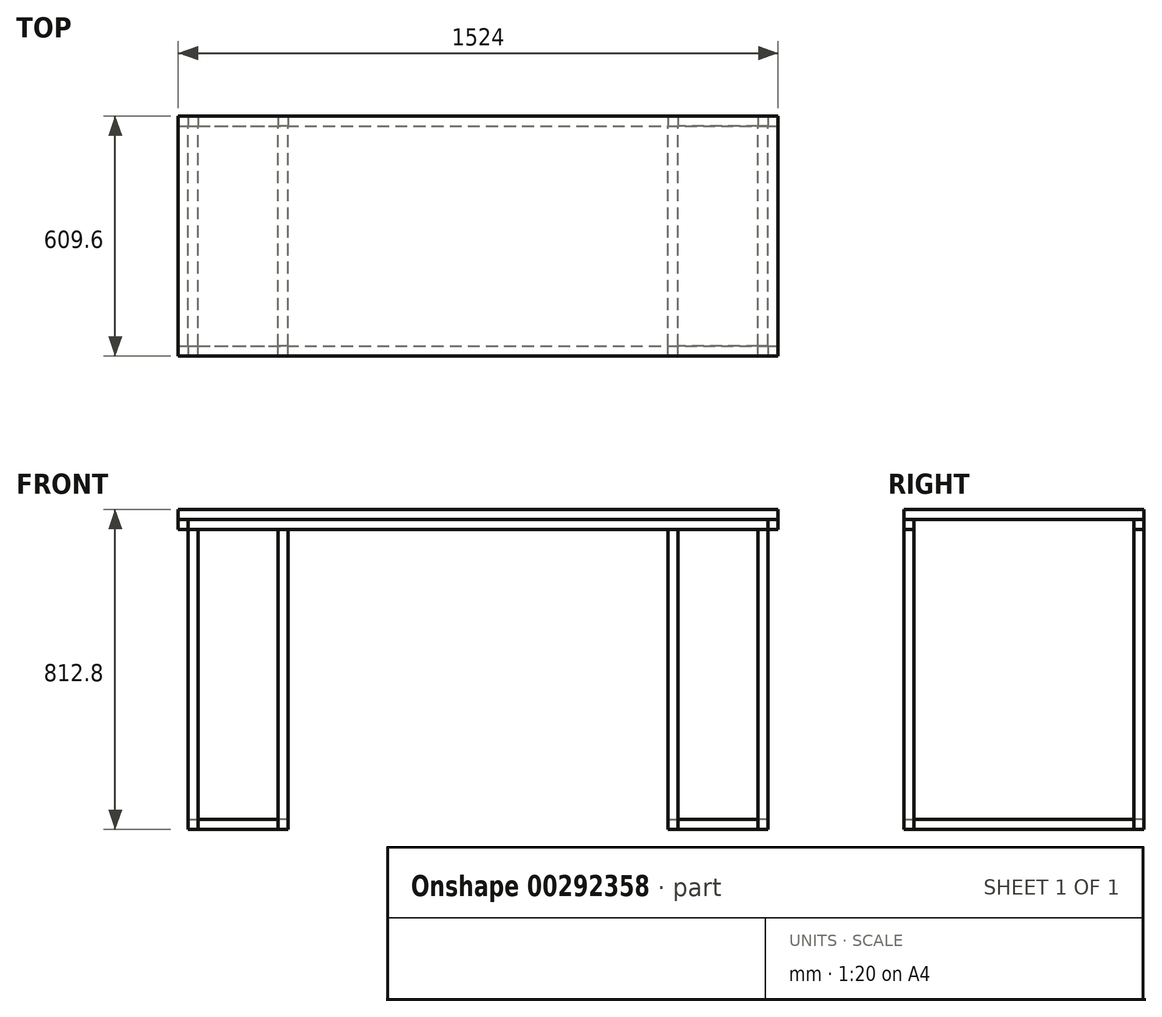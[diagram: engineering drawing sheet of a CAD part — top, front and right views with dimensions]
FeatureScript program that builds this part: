
annotation { "Feature Type Name" : "Feature", "Feature Type Description" : "" }
export const myFeature = defineFeature(function(context is Context, id is Id, definition is map)
    precondition{}
    {
        {
            var Q0;
            Q0=qCreatedBy(makeId("Top.planeOp"),FACE);
            var sketch = newSketch(context, id + "F0", { "sketchPlane" : qUnion([Q0])});
            skLineSegment(sketch, "E0.bottom", {"start": v(-1219.74, 156.93) * mm, "end": v(304.26, 156.93) * mm});
            skLineSegment(sketch, "E0.top", {"start": v(-1219.74, -452.67) * mm, "end": v(304.26, -452.67) * mm});
            skLineSegment(sketch, "E0.left", {"start": v(-1219.74, 156.93) * mm, "end": v(-1219.74, -452.67) * mm});
            skLineSegment(sketch, "E0.right", {"start": v(304.26, 156.93) * mm, "end": v(304.26, -452.67) * mm});
            skSolve(sketch);
        }
        {
            var Q0;
            Q0 = qSketchRegion(id + "F0", true);
            extrude(context, id + "F1", {"entities" : qUnion([Q0]), "depth" : 25.4 * mm});
        }
        {
            var Q0;
            Q0=makeQuery(id+"F1.opExtrude","CAP_FACE",FACE,{"disambiguationData":[OSD([sQuery(id+"F0.wireOp",EDGE,"E0.bottom"),sQuery(id+"F0.wireOp",EDGE,"E0.top"),sQuery(id+"F0.wireOp",EDGE,"E0.left"),sQuery(id+"F0.wireOp",EDGE,"E0.right")])],"isStart":true});
            var sketch = newSketch(context, id + "F2", { "sketchPlane" : qUnion([Q0])});
            skLineSegment(sketch, "E1.bottom", {"start": v(-1219.74, 452.67) * mm, "end": v(304.26, 452.67) * mm});
            skLineSegment(sketch, "E1.top", {"start": v(-1219.74, 427.27) * mm, "end": v(304.26, 427.27) * mm});
            skLineSegment(sketch, "E1.left", {"start": v(-1219.74, 452.67) * mm, "end": v(-1219.74, 427.27) * mm});
            skLineSegment(sketch, "E1.right", {"start": v(304.26, 452.67) * mm, "end": v(304.26, 427.27) * mm});
            skLineSegment(sketch, "E2.bottom", {"start": v(-1219.74, -156.93) * mm, "end": v(304.26, -156.93) * mm});
            skLineSegment(sketch, "E2.top", {"start": v(-1219.74, -131.53) * mm, "end": v(304.26, -131.53) * mm});
            skLineSegment(sketch, "E2.left", {"start": v(-1219.74, -156.93) * mm, "end": v(-1219.74, -131.53) * mm});
            skLineSegment(sketch, "E2.right", {"start": v(304.26, -156.93) * mm, "end": v(304.26, -131.53) * mm});
            skLineSegment(sketch, "E3.bottom", {"start": v(-1219.74, 427.27) * mm, "end": v(-1194.34, 427.27) * mm});
            skLineSegment(sketch, "E3.top", {"start": v(-1219.74, -131.53) * mm, "end": v(-1194.34, -131.53) * mm});
            skLineSegment(sketch, "E3.left", {"start": v(-1219.74, 427.27) * mm, "end": v(-1219.74, -131.53) * mm});
            skLineSegment(sketch, "E3.right", {"start": v(-1194.34, 427.27) * mm, "end": v(-1194.34, -131.53) * mm});
            skLineSegment(sketch, "E4.bottom", {"start": v(278.86, 427.27) * mm, "end": v(304.26, 427.27) * mm});
            skLineSegment(sketch, "E4.top", {"start": v(278.86, -131.53) * mm, "end": v(304.26, -131.53) * mm});
            skLineSegment(sketch, "E4.left", {"start": v(278.86, 427.27) * mm, "end": v(278.86, -131.53) * mm});
            skLineSegment(sketch, "E4.right", {"start": v(304.26, 427.27) * mm, "end": v(304.26, -131.53) * mm});
            skLineSegment(sketch, "E5", {"start": v(-1194.34, -131.53) * mm, "end": v(-1194.34, -156.93) * mm});
            skLineSegment(sketch, "E6", {"start": v(-1194.34, 427.27) * mm, "end": v(-1194.34, 452.67) * mm});
            skLineSegment(sketch, "E7", {"start": v(278.86, 427.27) * mm, "end": v(278.86, 452.67) * mm});
            skLineSegment(sketch, "E8", {"start": v(278.86, -131.53) * mm, "end": v(278.86, -156.93) * mm});
            skSolve(sketch);
        }
        {
            var Q0;
            Q0=makeQuery(id+"F2.imprint","IMPRINT",FACE,{"disambiguationData":[TD([[makeQuery(id+"F2.imprint","IMPRINT",EDGE,{"derivedFrom":sQuery(id+"F2.wireOp",EDGE,"E2.top")}),-1.0]])]});
            var Q1;
            Q1=makeQuery(id+"F2.imprint","IMPRINT",FACE,{"disambiguationData":[TD([[makeQuery(id+"F2.imprint","IMPRINT",EDGE,{"derivedFrom":sQuery(id+"F2.wireOp",EDGE,"E1.top")}),1.0]])]});
            extrude(context, id + "F3", {"entities" : qUnion([Q0, Q1]), "depth" : 25.4 * mm});
        }
        {
            var Q0;
            Q0=makeQuery(id+"F2.imprint","IMPRINT",FACE,{"disambiguationData":[TD([[makeQuery(id+"F2.imprint","IMPRINT",EDGE,{"derivedFrom":sQuery(id+"F2.wireOp",EDGE,"E3.bottom")}),-1.0]])]});
            var Q1;
            Q1=makeQuery(id+"F2.imprint","IMPRINT",FACE,{"disambiguationData":[TD([[makeQuery(id+"F2.imprint","IMPRINT",EDGE,{"derivedFrom":sQuery(id+"F2.wireOp",EDGE,"E4.bottom")}),-1.0]])]});
            var Q2;
            {var subQ0=sQuery(id+"F2.wireOp",EDGE,"E1.left");Q2=makeQuery(id+"F2.imprint","IMPRINT",FACE,{"disambiguationData":[TD([[makeQuery(id+"F2.imprint","IMPRINT",EDGE,{"derivedFrom":subQ0}),-1.0]])]});}
            var Q3;
            {var subQ0=sQuery(id+"F2.wireOp",EDGE,"E2.left");Q3=makeQuery(id+"F2.imprint","IMPRINT",FACE,{"disambiguationData":[TD([[makeQuery(id+"F2.imprint","IMPRINT",EDGE,{"derivedFrom":subQ0}),-1.0]])]});}
            var Q4;
            {var subQ0=sQuery(id+"F2.wireOp",EDGE,"E2.right");Q4=makeQuery(id+"F2.imprint","IMPRINT",FACE,{"disambiguationData":[TD([[makeQuery(id+"F2.imprint","IMPRINT",EDGE,{"derivedFrom":subQ0}),1.0]])]});}
            var Q5;
            {var subQ0=sQuery(id+"F2.wireOp",EDGE,"E1.right");Q5=makeQuery(id+"F2.imprint","IMPRINT",FACE,{"disambiguationData":[TD([[makeQuery(id+"F2.imprint","IMPRINT",EDGE,{"derivedFrom":subQ0}),1.0]])]});}
            extrude(context, id + "F4", {"entities" : qUnion([Q0, Q1, Q2, Q3, Q4, Q5]), "depth" : 25.4 * mm});
        }
        {
            var Q0;
            Q0=makeQuery(id+"F4.opExtrude","CAP_FACE",FACE,{"disambiguationData":[OSD([sQuery(id+"F2.wireOp",EDGE,"E1.bottom"),sQuery(id+"F2.wireOp",EDGE,"E1.right"),sQuery(id+"F2.wireOp",EDGE,"E2.bottom"),sQuery(id+"F2.wireOp",EDGE,"E2.right"),sQuery(id+"F2.wireOp",EDGE,"E4.left"),sQuery(id+"F2.wireOp",EDGE,"E4.right"),sQuery(id+"F2.wireOp",EDGE,"E7"),sQuery(id+"F2.wireOp",EDGE,"E8")])],"isStart":false});
            var sketch = newSketch(context, id + "F5", { "sketchPlane" : qUnion([Q0])});
            skLineSegment(sketch, "E9.bottom", {"start": v(-1194.34, 452.67) * mm, "end": v(-1168.94, 452.67) * mm});
            skLineSegment(sketch, "E9.top", {"start": v(-1194.34, 427.27) * mm, "end": v(-1168.94, 427.27) * mm});
            skLineSegment(sketch, "E9.left", {"start": v(-1194.34, 452.67) * mm, "end": v(-1194.34, 427.27) * mm});
            skLineSegment(sketch, "E9.right", {"start": v(-1168.94, 452.67) * mm, "end": v(-1168.94, 427.27) * mm});
            skPoint(sketch, "E10.0", {"position": v(-1219.74, 147.87) * mm});
            skPoint(sketch, "E11.0", {"position": v(304.26, 147.87) * mm});
            skPoint(sketch, "E12.0", {"position": v(-457.74, 452.67) * mm});
            skPoint(sketch, "E13.0", {"position": v(-457.74, -156.93) * mm});
            skLineSegment(sketch, "E14", {"start": v(-457.74, 452.67) * mm, "end": v(-457.74, -156.93) * mm, "construction": true});
            skLineSegment(sketch, "E15", {"start": v(304.26, 147.87) * mm, "end": v(-1219.74, 147.87) * mm, "construction": true});
            skLineSegment(sketch, "E16.MirrorCS", {"start": v(-1194.34, -131.53) * mm, "end": v(-1168.94, -131.53) * mm});
            skLineSegment(sketch, "E17.MirrorCS", {"start": v(-1194.34, -156.93) * mm, "end": v(-1168.94, -156.93) * mm});
            skLineSegment(sketch, "E18.MirrorCS", {"start": v(-1168.94, -156.93) * mm, "end": v(-1168.94, -131.53) * mm});
            skLineSegment(sketch, "E19.MirrorCS", {"start": v(-1194.34, -156.93) * mm, "end": v(-1194.34, -131.53) * mm});
            skLineSegment(sketch, "E20.MirrorCS", {"start": v(278.86, 427.27) * mm, "end": v(253.46, 427.27) * mm});
            skLineSegment(sketch, "E21.MirrorCS", {"start": v(278.86, 452.67) * mm, "end": v(278.86, 427.27) * mm});
            skLineSegment(sketch, "E22.MirrorCS", {"start": v(278.86, 452.67) * mm, "end": v(253.46, 452.67) * mm});
            skLineSegment(sketch, "E23.MirrorCS", {"start": v(253.46, 452.67) * mm, "end": v(253.46, 427.27) * mm});
            skLineSegment(sketch, "E24.MirrorCS", {"start": v(278.86, -131.53) * mm, "end": v(253.46, -131.53) * mm});
            skLineSegment(sketch, "E25.MirrorCS", {"start": v(278.86, -156.93) * mm, "end": v(278.86, -131.53) * mm});
            skLineSegment(sketch, "E26.MirrorCS", {"start": v(278.86, -156.93) * mm, "end": v(253.46, -156.93) * mm});
            skLineSegment(sketch, "E27.MirrorCS", {"start": v(253.46, -156.93) * mm, "end": v(253.46, -131.53) * mm});
            skLineSegment(sketch, "E28", {"start": v(-1168.94, 439.97) * mm, "end": v(-965.74, 439.97) * mm, "construction": true});
            skLineSegment(sketch, "E29", {"start": v(-1067.34, 439.97) * mm, "end": v(-1067.34, 504.42) * mm, "construction": true});
            skLineSegment(sketch, "E30.MirrorCS", {"start": v(-940.34, 452.67) * mm, "end": v(-965.74, 452.67) * mm});
            skLineSegment(sketch, "E31.MirrorCS", {"start": v(-940.34, 452.67) * mm, "end": v(-940.34, 427.27) * mm});
            skLineSegment(sketch, "E32.MirrorCS", {"start": v(-940.34, 427.27) * mm, "end": v(-965.74, 427.27) * mm});
            skLineSegment(sketch, "E33.MirrorCS", {"start": v(-965.74, 452.67) * mm, "end": v(-965.74, 427.27) * mm});
            skLineSegment(sketch, "E34.MirrorCS", {"start": v(-940.34, -131.53) * mm, "end": v(-965.74, -131.53) * mm});
            skLineSegment(sketch, "E35.MirrorCS", {"start": v(-940.34, -156.93) * mm, "end": v(-940.34, -131.53) * mm});
            skLineSegment(sketch, "E36.MirrorCS", {"start": v(-940.34, -156.93) * mm, "end": v(-965.74, -156.93) * mm});
            skLineSegment(sketch, "E37.MirrorCS", {"start": v(-965.74, -156.93) * mm, "end": v(-965.74, -131.53) * mm});
            skLineSegment(sketch, "E38.MirrorCS", {"start": v(24.86, 452.67) * mm, "end": v(50.26, 452.67) * mm});
            skLineSegment(sketch, "E39.MirrorCS", {"start": v(24.86, 427.27) * mm, "end": v(50.26, 427.27) * mm});
            skLineSegment(sketch, "E40.MirrorCS", {"start": v(50.26, 452.67) * mm, "end": v(50.26, 427.27) * mm});
            skLineSegment(sketch, "E41.MirrorCS", {"start": v(24.86, 452.67) * mm, "end": v(24.86, 427.27) * mm});
            skLineSegment(sketch, "E42.MirrorCS", {"start": v(24.86, -131.53) * mm, "end": v(50.26, -131.53) * mm});
            skLineSegment(sketch, "E43.MirrorCS", {"start": v(50.26, -156.93) * mm, "end": v(50.26, -131.53) * mm});
            skLineSegment(sketch, "E44.MirrorCS", {"start": v(24.86, -156.93) * mm, "end": v(50.26, -156.93) * mm});
            skLineSegment(sketch, "E45.MirrorCS", {"start": v(24.86, -156.93) * mm, "end": v(24.86, -131.53) * mm});
            skSolve(sketch);
        }
        {
            var Q0;
            Q0 = qSketchRegion(id + "F5", true);
            extrude(context, id + "F6", {"entities" : qUnion([Q0]), "depth" : 762 * mm});
        }
        {
            var Q0;
            Q0=makeQuery(id+"F6.opExtrude","CAP_FACE",FACE,{"disambiguationData":[OSD([sQuery(id+"F5.wireOp",EDGE,"E9.bottom"),sQuery(id+"F5.wireOp",EDGE,"E9.top"),sQuery(id+"F5.wireOp",EDGE,"E9.left"),sQuery(id+"F5.wireOp",EDGE,"E9.right")])],"isStart":false});
            var sketch = newSketch(context, id + "F7", { "sketchPlane" : qUnion([Q0])});
            skLineSegment(sketch, "E46.bottom", {"start": v(-1168.94, 452.67) * mm, "end": v(-965.74, 452.67) * mm});
            skLineSegment(sketch, "E46.top", {"start": v(-1168.94, 427.27) * mm, "end": v(-965.74, 427.27) * mm});
            skLineSegment(sketch, "E46.left", {"start": v(-1168.94, 452.67) * mm, "end": v(-1168.94, 427.27) * mm});
            skLineSegment(sketch, "E46.right", {"start": v(-965.74, 452.67) * mm, "end": v(-965.74, 427.27) * mm});
            skLineSegment(sketch, "E47.MirrorCS", {"start": v(253.46, 452.67) * mm, "end": v(50.26, 452.67) * mm});
            skLineSegment(sketch, "E48.MirrorCS", {"start": v(253.46, 427.27) * mm, "end": v(50.26, 427.27) * mm});
            skLineSegment(sketch, "E49.MirrorCS", {"start": v(50.26, 452.67) * mm, "end": v(50.26, 427.27) * mm});
            skLineSegment(sketch, "E50.MirrorCS", {"start": v(253.46, 452.67) * mm, "end": v(253.46, 427.27) * mm});
            skLineSegment(sketch, "E51.MirrorCS", {"start": v(-1168.94, -131.53) * mm, "end": v(-965.74, -131.53) * mm});
            skLineSegment(sketch, "E52.MirrorCS", {"start": v(-1168.94, -156.93) * mm, "end": v(-965.74, -156.93) * mm});
            skLineSegment(sketch, "E53.MirrorCS", {"start": v(-965.74, -156.93) * mm, "end": v(-965.74, -131.53) * mm});
            skLineSegment(sketch, "E54.MirrorCS", {"start": v(-1168.94, -156.93) * mm, "end": v(-1168.94, -131.53) * mm});
            skLineSegment(sketch, "E55.MirrorCS", {"start": v(253.46, -156.93) * mm, "end": v(50.26, -156.93) * mm});
            skLineSegment(sketch, "E56.MirrorCS", {"start": v(253.46, -131.53) * mm, "end": v(50.26, -131.53) * mm});
            skLineSegment(sketch, "E57.MirrorCS", {"start": v(50.26, -156.93) * mm, "end": v(50.26, -131.53) * mm});
            skLineSegment(sketch, "E58.MirrorCS", {"start": v(253.46, -156.93) * mm, "end": v(253.46, -131.53) * mm});
            skLineSegment(sketch, "E59.bottom", {"start": v(-1194.34, 427.27) * mm, "end": v(-1168.94, 427.27) * mm});
            skLineSegment(sketch, "E59.top", {"start": v(-1194.34, -131.53) * mm, "end": v(-1168.94, -131.53) * mm});
            skLineSegment(sketch, "E59.left", {"start": v(-1194.34, 427.27) * mm, "end": v(-1194.34, -131.53) * mm});
            skLineSegment(sketch, "E59.right", {"start": v(-1168.94, 427.27) * mm, "end": v(-1168.94, -131.53) * mm});
            skLineSegment(sketch, "E60.MirrorCS", {"start": v(-965.74, 427.27) * mm, "end": v(-965.74, -131.53) * mm});
            skLineSegment(sketch, "E61.MirrorCS", {"start": v(-940.34, 427.27) * mm, "end": v(-940.34, -131.53) * mm});
            skLineSegment(sketch, "E62.MirrorCS", {"start": v(-940.34, 427.27) * mm, "end": v(-965.74, 427.27) * mm});
            skLineSegment(sketch, "E63.MirrorCS", {"start": v(-940.34, -131.53) * mm, "end": v(-965.74, -131.53) * mm});
            skLineSegment(sketch, "E64.MirrorCS", {"start": v(278.86, 427.27) * mm, "end": v(278.86, -131.53) * mm});
            skLineSegment(sketch, "E65.MirrorCS", {"start": v(253.46, 427.27) * mm, "end": v(253.46, -131.53) * mm});
            skLineSegment(sketch, "E66.MirrorCS", {"start": v(50.26, 427.27) * mm, "end": v(50.26, -131.53) * mm});
            skLineSegment(sketch, "E67.MirrorCS", {"start": v(24.86, 427.27) * mm, "end": v(24.86, -131.53) * mm});
            skLineSegment(sketch, "E68.MirrorCS", {"start": v(24.86, 427.27) * mm, "end": v(50.26, 427.27) * mm});
            skLineSegment(sketch, "E69.MirrorCS", {"start": v(24.86, -131.53) * mm, "end": v(50.26, -131.53) * mm});
            skLineSegment(sketch, "E70.MirrorCS", {"start": v(278.86, -131.53) * mm, "end": v(253.46, -131.53) * mm});
            skLineSegment(sketch, "E71.MirrorCS", {"start": v(278.86, 427.27) * mm, "end": v(253.46, 427.27) * mm});
            skSolve(sketch);
        }
        {
            var Q0;
            Q0=makeQuery(id+"F7.imprint","IMPRINT",FACE,{"disambiguationData":[TD([[makeQuery(id+"F7.imprint","IMPRINT",EDGE,{"derivedFrom":sQuery(id+"F7.wireOp",EDGE,"E59.bottom")}),-1.0]])]});
            var Q1;
            Q1=makeQuery(id+"F7.imprint","IMPRINT",FACE,{"disambiguationData":[TD([[makeQuery(id+"F7.imprint","IMPRINT",EDGE,{"derivedFrom":sQuery(id+"F7.wireOp",EDGE,"E46.bottom")}),-1.0]])]});
            var Q2;
            Q2=makeQuery(id+"F7.imprint","IMPRINT",FACE,{"disambiguationData":[TD([[makeQuery(id+"F7.imprint","IMPRINT",EDGE,{"derivedFrom":sQuery(id+"F7.wireOp",EDGE,"E60.MirrorCS")}),1.0]])]});
            var Q3;
            Q3=makeQuery(id+"F7.imprint","IMPRINT",FACE,{"disambiguationData":[TD([[makeQuery(id+"F7.imprint","IMPRINT",EDGE,{"derivedFrom":sQuery(id+"F7.wireOp",EDGE,"E51.MirrorCS")}),-1.0]])]});
            var Q4;
            Q4=makeQuery(id+"F7.imprint","IMPRINT",FACE,{"disambiguationData":[TD([[makeQuery(id+"F7.imprint","IMPRINT",EDGE,{"derivedFrom":sQuery(id+"F7.wireOp",EDGE,"E66.MirrorCS")}),-1.0]])]});
            var Q5;
            Q5=makeQuery(id+"F7.imprint","IMPRINT",FACE,{"disambiguationData":[TD([[makeQuery(id+"F7.imprint","IMPRINT",EDGE,{"derivedFrom":sQuery(id+"F7.wireOp",EDGE,"E47.MirrorCS")}),1.0]])]});
            var Q6;
            Q6=makeQuery(id+"F7.imprint","IMPRINT",FACE,{"disambiguationData":[TD([[makeQuery(id+"F7.imprint","IMPRINT",EDGE,{"derivedFrom":sQuery(id+"F7.wireOp",EDGE,"E55.MirrorCS")}),-1.0]])]});
            var Q7;
            Q7=makeQuery(id+"F7.imprint","IMPRINT",FACE,{"disambiguationData":[TD([[makeQuery(id+"F7.imprint","IMPRINT",EDGE,{"derivedFrom":sQuery(id+"F7.wireOp",EDGE,"E64.MirrorCS")}),-1.0]])]});
            extrude(context, id + "F8", {"entities" : qUnion([Q0, Q1, Q2, Q3, Q4, Q5, Q6, Q7]), "oppositeDirection" : true, "depth" : 25.4 * mm});
        }
    });
